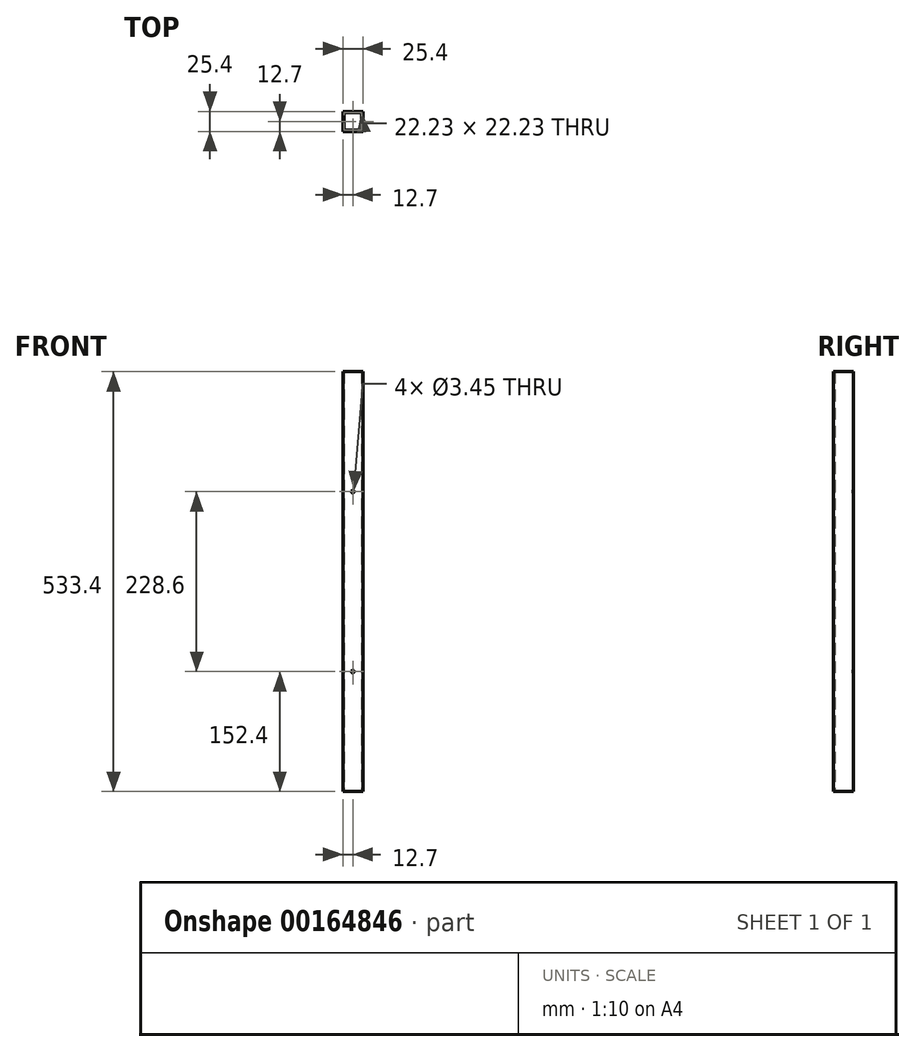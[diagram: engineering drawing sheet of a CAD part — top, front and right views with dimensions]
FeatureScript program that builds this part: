
annotation { "Feature Type Name" : "Feature", "Feature Type Description" : "" }
export const myFeature = defineFeature(function(context is Context, id is Id, definition is map)
    precondition{}
    {
        {
            var Q0;
            Q0=qCreatedBy(makeId("Top.planeOp"),FACE);
            var sketch = newSketch(context, id + "F0", { "sketchPlane" : qUnion([Q0])});
            skLineSegment(sketch, "E0.bottom", {"start": v(11.11, -11.11) * mm, "end": v(-11.11, -11.11) * mm});
            skLineSegment(sketch, "E0.top", {"start": v(11.11, 11.11) * mm, "end": v(-11.11, 11.11) * mm});
            skLineSegment(sketch, "E0.left", {"start": v(11.11, -11.11) * mm, "end": v(11.11, 11.11) * mm});
            skLineSegment(sketch, "E0.right", {"start": v(-11.11, -11.11) * mm, "end": v(-11.11, 11.11) * mm});
            skPoint(sketch, "E0.middle", {"position": v(0, 0) * mm});
            skLineSegment(sketch, "E1.bottom", {"start": v(12.7, -12.7) * mm, "end": v(-12.7, -12.7) * mm});
            skLineSegment(sketch, "E1.top", {"start": v(12.7, 12.7) * mm, "end": v(-12.7, 12.7) * mm});
            skLineSegment(sketch, "E1.left", {"start": v(12.7, -12.7) * mm, "end": v(12.7, 12.7) * mm});
            skLineSegment(sketch, "E1.right", {"start": v(-12.7, -12.7) * mm, "end": v(-12.7, 12.7) * mm});
            skSolve(sketch);
        }
        {
            var Q0;
            Q0=qSketchRegion(id+"F0",true);
            extrude(context, id + "F1", {"entities" : qUnion([Q0]), "depth" : 533.4 * mm});
        }
        {
            var Q0;
            Q0=makeQuery(id+"F1.opExtrude","SWEPT_FACE",FACE,{"disambiguationData":[OSD([sQuery(id+"F0.wireOp",EDGE,"E1.bottom")])]});
            var sketch = newSketch(context, id + "F2", { "sketchPlane" : qUnion([Q0])});
            skLineSegment(sketch, "E2", {"start": v(0, 0) * mm, "end": v(0, 152.4) * mm, "construction": true});
            skLineSegment(sketch, "E3", {"start": v(0, 152.4) * mm, "end": v(0, 381) * mm, "construction": true});
            skLineSegment(sketch, "E4", {"start": v(0, 533.4) * mm, "end": v(0, 381) * mm, "construction": true});
            skCircle(sketch, "E5", {"center": v(0, 152.4) * mm, "radius": 1.73 * mm});
            skCircle(sketch, "E6", {"center": v(0, 381) * mm, "radius": 1.73 * mm});
            skSolve(sketch);
        }
        {
            var Q0;
            Q0=qSketchRegion(id+"F2",true);
            var Q1;
            Q1=makeQuery(id+"F1.opExtrude","SWEPT_FACE",FACE,{"disambiguationData":[OSD([sQuery(id+"F0.wireOp",EDGE,"E1.top")])]});
            extrude(context, id + "F3", {"entities" : qUnion([Q0]), "operationType" : NewBodyOperationType.REMOVE, "endBound" : BoundingType.UP_TO_SURFACE, "oppositeDirection" : true, "endBoundEntityFace" : qUnion([Q1]), "depth" : 25.4 * mm});
        }
    });
